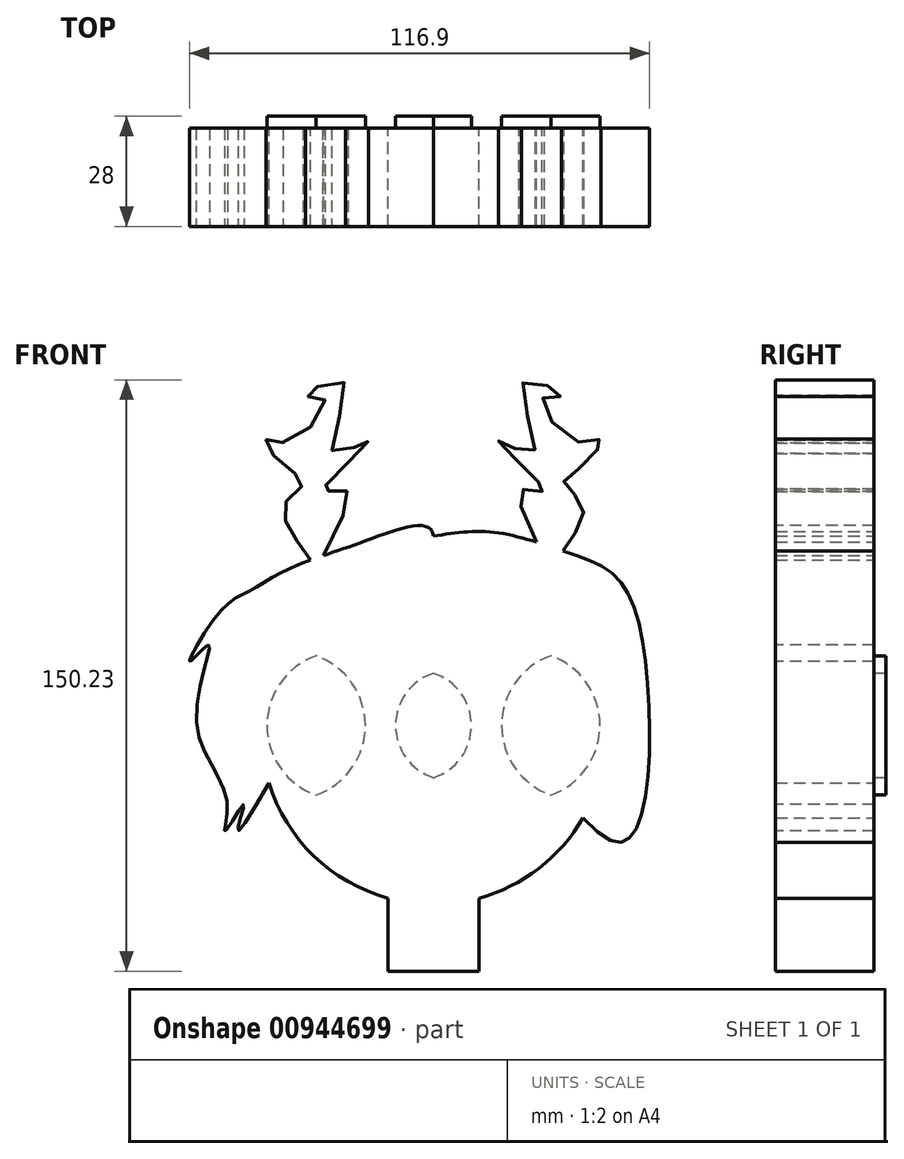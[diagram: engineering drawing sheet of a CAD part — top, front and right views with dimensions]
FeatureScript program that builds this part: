
annotation { "Feature Type Name" : "Feature", "Feature Type Description" : "" }
export const myFeature = defineFeature(function(context is Context, id is Id, definition is map)
    precondition{}
    {
        {
            var Q0;
            Q0=qCreatedBy(makeId("Front.planeOp"),FACE);
            var sketch = newSketch(context, id + "F0", { "sketchPlane" : qUnion([Q0])});
            skFitSpline(sketch, "E0", {"points": [v(0, 74.85) * mm, v(-24.1, 35.74) * mm, v(-22.09, 45.58) * mm, v(-49.6, 0) * mm, v(-48.19, 6.63) * mm, v(-52.8, 0) * mm, v(-52.4, 7.23) * mm, v(-60.24, 27.9) * mm, v(-57.22, 47.18) * mm, v(-61.84, 42.97) * mm, v(-54.41, 55.41) * mm, v(-46.58, 61.04) * mm, v(-37.35, 66.26) * mm, v(-17.67, 73.48) * mm, v(0, 74.85) * mm]});
            skFitSpline(sketch, "E1", {"points": [v(-2.75, 65.67) * mm, v(46.23, -2.88) * mm, v(52.85, 4.25) * mm, v(53.69, 44.45) * mm, v(46.51, 64.34) * mm, v(33.32, 70.96) * mm, v(15.2, 75.82) * mm, v(0, 74.85) * mm], "startDerivative": vector(227.88, -384.27) * mm, "endDerivative": vector(-133.99, -20.94) * mm});
            skFitSpline(sketch, "E2", {"points": [v(-31.19, 68.78) * mm, v(-36.37, 76.27) * mm, v(-37.7, 83.15) * mm, v(-33.12, 88.32) * mm, v(-39.05, 93.67) * mm, v(-42.49, 99.4) * mm, v(-36.37, 98.83) * mm, v(-27.94, 110.1) * mm, v(-32.55, 110.49) * mm, v(-22.99, 114.12) * mm, v(-25.47, 96.15) * mm, v(-16.68, 99.21) * mm, v(-24.14, 91.18) * mm, v(-27.94, 86.21) * mm, v(-22.42, 86.6) * mm, v(-27.94, 69.92) * mm], "startDerivative": vector(-81.57, 108.27) * mm, "endDerivative": vector(-127.31, -248.08) * mm});
            skFitSpline(sketch, "E3.MirrorCS", {"points": [v(31.19, 68.78) * mm, v(36.37, 76.27) * mm, v(37.7, 83.15) * mm, v(33.12, 88.32) * mm, v(39.05, 93.67) * mm, v(42.49, 99.4) * mm, v(36.37, 98.83) * mm, v(27.94, 110.1) * mm, v(32.55, 110.49) * mm, v(22.99, 114.12) * mm, v(25.47, 96.15) * mm, v(16.68, 99.21) * mm, v(24.14, 91.18) * mm, v(27.94, 86.21) * mm, v(22.42, 86.6) * mm, v(27.94, 69.92) * mm], "startDerivative": vector(81.57, 108.27) * mm, "endDerivative": vector(127.31, -248.08) * mm});
            skArc(sketch, "E4", {"start": v(0, 13.47) * mm, "mid": v(9.63, 26.74) * mm, "end": v(0, 40.01) * mm});
            skArc(sketch, "E5.MirrorCS", {"start": v(0, 13.47) * mm, "mid": v(-9.63, 26.74) * mm, "end": v(0, 40.01) * mm});
            skCircle(sketch, "E6", {"center": v(0, 25.12) * mm, "radius": 43.82 * mm});
            skPoint(sketch, "E7.endSnap0", {"position": v(-9.63, 26.74) * mm});
            skArc(sketch, "E8", {"start": v(29.81, 9.03) * mm, "mid": v(42.3, 26.74) * mm, "end": v(29.81, 44.45) * mm});
            skArc(sketch, "E9.MirrorCS", {"start": v(29.81, 9.03) * mm, "mid": v(17.32, 26.74) * mm, "end": v(29.81, 44.45) * mm});
            skArc(sketch, "E10.MirrorCS", {"start": v(-29.81, 9.03) * mm, "mid": v(-42.3, 26.74) * mm, "end": v(-29.81, 44.45) * mm});
            skArc(sketch, "E11.MirrorCS", {"start": v(-29.82, 9.03) * mm, "mid": v(-17.32, 26.74) * mm, "end": v(-29.82, 44.45) * mm});
            skLineSegment(sketch, "E12", {"start": v(-11.56, -17.15) * mm, "end": v(-11.56, -35.7) * mm});
            skLineSegment(sketch, "E13.MirrorCS", {"start": v(11.56, -17.15) * mm, "end": v(11.56, -35.7) * mm});
            skLineSegment(sketch, "E14", {"start": v(-11.56, -35.7) * mm, "end": v(11.56, -35.7) * mm});
            skLineSegment(sketch, "E15", {"start": v(-58.23, 40.96) * mm, "end": v(-63.12, 26.74) * mm});
            skSolve(sketch);
        }
        {
            var Q0;
            {var subQ0=sQuery(id+"F0.wireOp",EDGE,"E11.MirrorCS");var subQ3=sQuery(id+"F0.wireOp",EDGE,"E0");var subQ4=makeQuery(id+"F0.imprint","INTERSECT",VERTEX,{"disambiguationData":[OD(0.0)],"derivedFrom":[subQ3,subQ0]});Q0=makeQuery(id+"F0.imprint","IMPRINT",FACE,{"disambiguationData":[TD([[makeQuery(id+"F0.imprint","IMPRINT",EDGE,{"disambiguationData":[TD([[subQ4,-1.0]])],"derivedFrom":subQ3}),1.0]])]});}
            var Q1;
            {var subQ0=sQuery(id+"F0.wireOp",EDGE,"E11.MirrorCS");var subQ1=sQuery(id+"F0.wireOp",EDGE,"E0");var subQ2=makeQuery(id+"F0.imprint","INTERSECT",VERTEX,{"disambiguationData":[OD(2.0)],"derivedFrom":[subQ1,subQ0]});Q1=makeQuery(id+"F0.imprint","IMPRINT",FACE,{"disambiguationData":[TD([[makeQuery(id+"F0.imprint","IMPRINT",EDGE,{"disambiguationData":[TD([[subQ2,-1.0]])],"derivedFrom":subQ1}),-1.0]])]});}
            var Q2;
            Q2=makeQuery(id+"F0.imprint","IMPRINT",FACE,{"disambiguationData":[TD([[makeQuery(id+"F0.imprint","IMPRINT",EDGE,{"derivedFrom":sQuery(id+"F0.wireOp",EDGE,"E4")}),1.0]])]});
            var Q3;
            {var subQ0=sQuery(id+"F0.wireOp",EDGE,"E9.MirrorCS");var subQ1=sQuery(id+"F0.wireOp",EDGE,"E1");var subQ2=makeQuery(id+"F0.imprint","INTERSECT",VERTEX,{"derivedFrom":[subQ1,subQ0]});Q3=makeQuery(id+"F0.imprint","IMPRINT",FACE,{"disambiguationData":[TD([[makeQuery(id+"F0.imprint","IMPRINT",EDGE,{"disambiguationData":[TD([[subQ2,-1.0]])],"derivedFrom":subQ1}),-1.0]])]});}
            var Q4;
            {var subQ0=sQuery(id+"F0.wireOp",EDGE,"E9.MirrorCS");var subQ1=sQuery(id+"F0.wireOp",EDGE,"E1");var subQ2=makeQuery(id+"F0.imprint","INTERSECT",VERTEX,{"derivedFrom":[subQ1,subQ0]});Q4=makeQuery(id+"F0.imprint","IMPRINT",FACE,{"disambiguationData":[TD([[makeQuery(id+"F0.imprint","IMPRINT",EDGE,{"disambiguationData":[TD([[subQ2,-1.0]])],"derivedFrom":subQ1}),1.0]])]});}
            var Q5;
            Q5=makeQuery(id+"F0.imprint","IMPRINT",FACE,{"disambiguationData":[TD([[makeQuery(id+"F0.imprint","IMPRINT",EDGE,{"derivedFrom":sQuery(id+"F0.wireOp",EDGE,"E4")}),-1.0]])]});
            var Q6;
            {var subQ1=sQuery(id+"F0.wireOp",EDGE,"E0");var subQ4=makeQuery(id+"F0.imprint","IMPRINT",VERTEX,{"derivedFrom":subQ1});Q6=makeQuery(id+"F0.imprint","IMPRINT",FACE,{"disambiguationData":[TD([[makeQuery(id+"F0.imprint","IMPRINT",EDGE,{"disambiguationData":[TD([[subQ4,1.0]])],"derivedFrom":subQ1}),-1.0]])]});}
            var Q7;
            {var subQ1=sQuery(id+"F0.wireOp",EDGE,"E0");var subQ4=makeQuery(id+"F0.imprint","INTERSECT",VERTEX,{"disambiguationData":[OD(0.0)],"derivedFrom":[subQ1,sQuery(id+"F0.wireOp",EDGE,"E1")]});Q7=makeQuery(id+"F0.imprint","IMPRINT",FACE,{"disambiguationData":[TD([[makeQuery(id+"F0.imprint","IMPRINT",EDGE,{"disambiguationData":[TD([[subQ4,1.0]])],"derivedFrom":subQ1}),-1.0]])]});}
            var Q8;
            {var subQ0=sQuery(id+"F0.wireOp",EDGE,"E11.MirrorCS");var subQ1=sQuery(id+"F0.wireOp",EDGE,"E0");var subQ2=makeQuery(id+"F0.imprint","INTERSECT",VERTEX,{"disambiguationData":[OD(0.0)],"derivedFrom":[subQ1,subQ0]});Q8=makeQuery(id+"F0.imprint","IMPRINT",FACE,{"disambiguationData":[TD([[makeQuery(id+"F0.imprint","IMPRINT",EDGE,{"disambiguationData":[TD([[subQ2,-1.0]])],"derivedFrom":subQ1}),-1.0]])]});}
            var Q9;
            {var subQ0=sQuery(id+"F0.wireOp",EDGE,"E11.MirrorCS");var subQ1=sQuery(id+"F0.wireOp",EDGE,"E0");var subQ2=makeQuery(id+"F0.imprint","INTERSECT",VERTEX,{"disambiguationData":[OD(1.0)],"derivedFrom":[subQ1,subQ0]});Q9=makeQuery(id+"F0.imprint","IMPRINT",FACE,{"disambiguationData":[TD([[makeQuery(id+"F0.imprint","IMPRINT",EDGE,{"disambiguationData":[TD([[subQ2,-1.0]])],"derivedFrom":subQ1}),1.0]])]});}
            var Q10;
            {var subQ1=sQuery(id+"F0.wireOp",EDGE,"E1");var subQ3=sQuery(id+"F0.wireOp",EDGE,"E0");var subQ7=makeQuery(id+"F0.imprint","INTERSECT",VERTEX,{"disambiguationData":[OD(0.0)],"derivedFrom":[subQ3,subQ1]});Q10=makeQuery(id+"F0.imprint","IMPRINT",FACE,{"disambiguationData":[TD([[makeQuery(id+"F0.imprint","IMPRINT",EDGE,{"disambiguationData":[TD([[subQ7,1.0]])],"derivedFrom":subQ3}),1.0]])]});}
            var Q11;
            {var subQ0=sQuery(id+"F0.wireOp",EDGE,"E1");var subQ1=sQuery(id+"F0.wireOp",EDGE,"E0");var subQ2=makeQuery(id+"F0.imprint","INTERSECT",VERTEX,{"disambiguationData":[OD(1.0)],"derivedFrom":[subQ1,subQ0]});Q11=makeQuery(id+"F0.imprint","IMPRINT",FACE,{"disambiguationData":[TD([[makeQuery(id+"F0.imprint","IMPRINT",EDGE,{"disambiguationData":[TD([[subQ2,-1.0]])],"derivedFrom":subQ1}),1.0]])]});}
            var Q12;
            {var subQ0=sQuery(id+"F0.wireOp",EDGE,"E12");Q12=makeQuery(id+"F0.imprint","IMPRINT",FACE,{"disambiguationData":[TD([[makeQuery(id+"F0.imprint","IMPRINT",EDGE,{"derivedFrom":subQ0}),1.0]])]});}
            var Q13;
            {var subQ0=sQuery(id+"F0.wireOp",EDGE,"E2");Q13=makeQuery(id+"F0.imprint","IMPRINT",FACE,{"disambiguationData":[TD([[makeQuery(id+"F0.imprint","IMPRINT",EDGE,{"derivedFrom":subQ0}),-1.0]])]});}
            var Q14;
            {var subQ0=sQuery(id+"F0.wireOp",EDGE,"E3.MirrorCS");var subQ1=sQuery(id+"F0.wireOp",EDGE,"E1");var subQ2=makeQuery(id+"F0.imprint","INTERSECT",VERTEX,{"disambiguationData":[OD(0.0)],"derivedFrom":[subQ1,subQ0]});Q14=makeQuery(id+"F0.imprint","IMPRINT",FACE,{"disambiguationData":[TD([[makeQuery(id+"F0.imprint","IMPRINT",EDGE,{"disambiguationData":[TD([[subQ2,-1.0]])],"derivedFrom":subQ1}),-1.0]])]});}
            extrude(context, id + "F1", {"entities" : qUnion([Q0, Q1, Q2, Q3, Q4, Q5, Q6, Q7, Q8, Q9, Q10, Q11, Q12, Q13, Q14]), "depth" : 25 * mm, "offsetDistance" : 25.4 * mm});
        }
        {
            var Q0;
            {var subQ0=sQuery(id+"F0.wireOp",EDGE,"E9.MirrorCS");var subQ1=sQuery(id+"F0.wireOp",EDGE,"E1");var subQ2=makeQuery(id+"F0.imprint","INTERSECT",VERTEX,{"derivedFrom":[subQ1,subQ0]});Q0=makeQuery(id+"F0.imprint","IMPRINT",FACE,{"disambiguationData":[TD([[makeQuery(id+"F0.imprint","IMPRINT",EDGE,{"disambiguationData":[TD([[subQ2,-1.0]])],"derivedFrom":subQ1}),1.0]])]});}
            var Q1;
            {var subQ0=sQuery(id+"F0.wireOp",EDGE,"E9.MirrorCS");var subQ1=sQuery(id+"F0.wireOp",EDGE,"E1");var subQ2=makeQuery(id+"F0.imprint","INTERSECT",VERTEX,{"derivedFrom":[subQ1,subQ0]});Q1=makeQuery(id+"F0.imprint","IMPRINT",FACE,{"disambiguationData":[TD([[makeQuery(id+"F0.imprint","IMPRINT",EDGE,{"disambiguationData":[TD([[subQ2,-1.0]])],"derivedFrom":subQ1}),-1.0]])]});}
            var Q2;
            Q2=makeQuery(id+"F0.imprint","IMPRINT",FACE,{"disambiguationData":[TD([[makeQuery(id+"F0.imprint","IMPRINT",EDGE,{"derivedFrom":sQuery(id+"F0.wireOp",EDGE,"E4")}),1.0]])]});
            var Q3;
            {var subQ0=sQuery(id+"F0.wireOp",EDGE,"E11.MirrorCS");var subQ3=sQuery(id+"F0.wireOp",EDGE,"E0");var subQ4=makeQuery(id+"F0.imprint","INTERSECT",VERTEX,{"disambiguationData":[OD(0.0)],"derivedFrom":[subQ3,subQ0]});Q3=makeQuery(id+"F0.imprint","IMPRINT",FACE,{"disambiguationData":[TD([[makeQuery(id+"F0.imprint","IMPRINT",EDGE,{"disambiguationData":[TD([[subQ4,-1.0]])],"derivedFrom":subQ3}),1.0]])]});}
            var Q4;
            {var subQ0=sQuery(id+"F0.wireOp",EDGE,"E11.MirrorCS");var subQ1=sQuery(id+"F0.wireOp",EDGE,"E0");var subQ2=makeQuery(id+"F0.imprint","INTERSECT",VERTEX,{"disambiguationData":[OD(2.0)],"derivedFrom":[subQ1,subQ0]});Q4=makeQuery(id+"F0.imprint","IMPRINT",FACE,{"disambiguationData":[TD([[makeQuery(id+"F0.imprint","IMPRINT",EDGE,{"disambiguationData":[TD([[subQ2,-1.0]])],"derivedFrom":subQ1}),-1.0]])]});}
            var Q5;
            {var subQ0=sQuery(id+"F0.wireOp",EDGE,"E11.MirrorCS");var subQ1=sQuery(id+"F0.wireOp",EDGE,"E0");var subQ2=makeQuery(id+"F0.imprint","INTERSECT",VERTEX,{"disambiguationData":[OD(0.0)],"derivedFrom":[subQ1,subQ0]});Q5=makeQuery(id+"F0.imprint","IMPRINT",FACE,{"disambiguationData":[TD([[makeQuery(id+"F0.imprint","IMPRINT",EDGE,{"disambiguationData":[TD([[subQ2,-1.0]])],"derivedFrom":subQ1}),-1.0]])]});}
            extrude(context, id + "F2", {"entities" : qUnion([Q0, Q1, Q2, Q3, Q4, Q5]), "operationType" : NewBodyOperationType.ADD, "depth" : 0 * mm, "offsetDistance" : 25.4 * mm, "hasSecondDirection" : true, "secondDirectionOppositeDirection" : true, "secondDirectionDepth" : 3 * mm});
        }
    });
